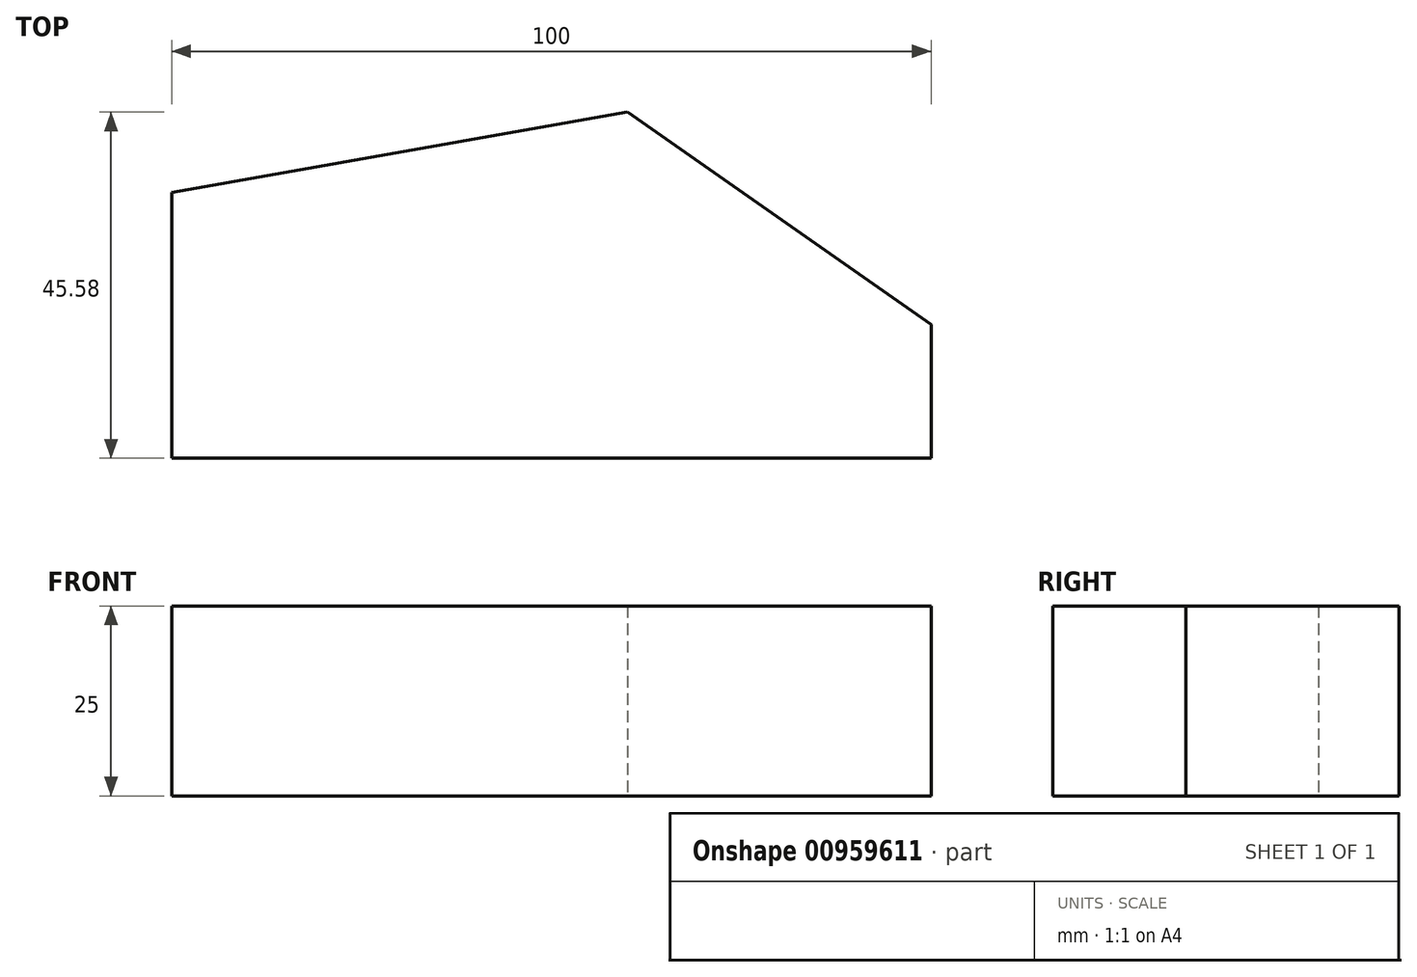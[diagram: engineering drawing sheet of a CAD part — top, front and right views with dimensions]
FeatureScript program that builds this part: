
annotation { "Feature Type Name" : "Feature", "Feature Type Description" : "" }
export const myFeature = defineFeature(function(context is Context, id is Id, definition is map)
    precondition{}
    {
        {
            var Q0;
            Q0=qCreatedBy(makeId("Top.planeOp"),FACE);
            var sketch = newSketch(context, id + "F0", { "sketchPlane" : qUnion([Q0])});
            skLineSegment(sketch, "E0", {"start": v(0, 0) * mm, "end": v(100, 0) * mm});
            skLineSegment(sketch, "E1", {"start": v(100, 17.57) * mm, "end": v(60, 45.58) * mm});
            skLineSegment(sketch, "E2", {"start": v(100, 17.57) * mm, "end": v(100, 0) * mm});
            skLineSegment(sketch, "E3", {"start": v(60, 45.58) * mm, "end": v(0, 35) * mm});
            skLineSegment(sketch, "E4", {"start": v(0, 35) * mm, "end": v(0, 0) * mm});
            skSolve(sketch);
        }
        {
            var Q0;
            Q0=makeQuery(id+"F0.imprint","IMPRINT",FACE,{"disambiguationData":[TD([[makeQuery(id+"F0.imprint","IMPRINT",EDGE,{"derivedFrom":sQuery(id+"F0.wireOp",EDGE,"E0")}),1.0]])]});
            extrude(context, id + "F1", {"entities" : qUnion([Q0]), "depth" : 25 * mm, "offsetDistance" : 25 * mm});
        }
    });
